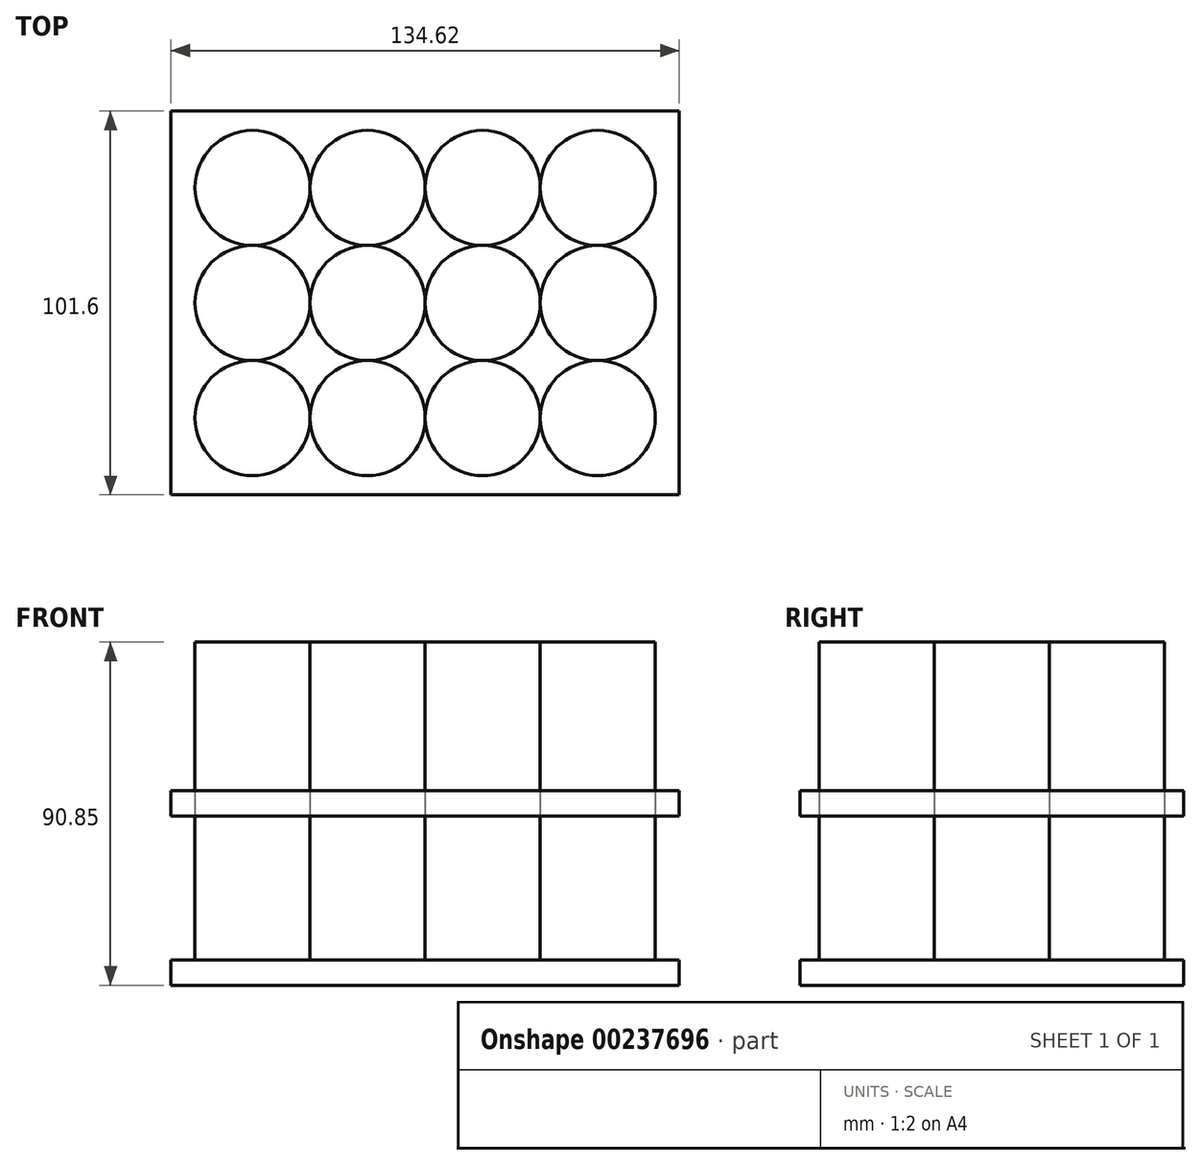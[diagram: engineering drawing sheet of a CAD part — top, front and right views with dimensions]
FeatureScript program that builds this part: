
annotation { "Feature Type Name" : "Feature", "Feature Type Description" : "" }
export const myFeature = defineFeature(function(context is Context, id is Id, definition is map)
    precondition{}
    {
        {
            var Q0;
            Q0=qCreatedBy(makeId("Top.planeOp"),FACE);
            var sketch = newSketch(context, id + "F0", { "sketchPlane" : qUnion([Q0])});
            skCircle(sketch, "E0", {"center": v(-45.72, -30.48) * mm, "radius": 15.24 * mm});
            skCircle(sketch, "E1", {"center": v(-15.24, -30.48) * mm, "radius": 15.24 * mm});
            skCircle(sketch, "E2", {"center": v(15.24, -30.48) * mm, "radius": 15.24 * mm});
            skCircle(sketch, "E3", {"center": v(-45.72, 0) * mm, "radius": 15.24 * mm});
            skCircle(sketch, "E4", {"center": v(-15.24, 0) * mm, "radius": 15.24 * mm});
            skCircle(sketch, "E5", {"center": v(15.24, 0) * mm, "radius": 15.24 * mm});
            skLineSegment(sketch, "E6", {"start": v(-45.72, 0) * mm, "end": v(-45.72, -30.48) * mm, "construction": true});
            skCircle(sketch, "E7", {"center": v(-45.72, 30.48) * mm, "radius": 15.24 * mm});
            skCircle(sketch, "E8", {"center": v(-15.24, 30.48) * mm, "radius": 15.24 * mm});
            skCircle(sketch, "E9", {"center": v(15.24, 30.48) * mm, "radius": 15.24 * mm});
            skLineSegment(sketch, "E10", {"start": v(-45.72, 30.48) * mm, "end": v(-45.72, 0) * mm, "construction": true});
            skCircle(sketch, "E11", {"center": v(45.72, -30.48) * mm, "radius": 15.24 * mm});
            skCircle(sketch, "E12", {"center": v(45.72, 0) * mm, "radius": 15.24 * mm});
            skCircle(sketch, "E13", {"center": v(45.72, 30.48) * mm, "radius": 15.24 * mm});
            skLineSegment(sketch, "E14", {"start": v(45.72, 30.48) * mm, "end": v(45.72, -30.48) * mm, "construction": true});
            skLineSegment(sketch, "E15", {"start": v(-45.72, 0) * mm, "end": v(45.72, 0) * mm, "construction": true});
            skLineSegment(sketch, "E16", {"start": v(-45.72, 30.48) * mm, "end": v(45.72, 30.48) * mm, "construction": true});
            skLineSegment(sketch, "E17", {"start": v(-45.72, -30.48) * mm, "end": v(45.72, -30.48) * mm, "construction": true});
            skSolve(sketch);
        }
        {
            var Q0;
            {var subQ0=sQuery(id+"F0.wireOp",EDGE,"ICpDPUjX-ivMe-23Ei-ieje-qIsjfVPonkm3");var subQ1=makeQuery(id+"F0.imprint","INTERSECT",VERTEX,{"derivedFrom":[subQ0,sQuery(id+"F0.wireOp",EDGE,"1585de0c-b4fc-4455-9636-1ccd38715f07")]});Q0=makeQuery(id+"F0.imprint","IMPRINT",FACE,{"disambiguationData":[TD([[makeQuery(id+"F0.imprint","IMPRINT",EDGE,{"disambiguationData":[TD([[subQ1,-1.0]])],"derivedFrom":subQ0}),1.0]])]});}
            var Q1;
            {var subQ0=sQuery(id+"F0.wireOp",EDGE,"1585de0c-b4fc-4455-9636-1ccd38715f07");var subQ1=makeQuery(id+"F0.imprint","INTERSECT",VERTEX,{"derivedFrom":[sQuery(id+"F0.wireOp",EDGE,"ICpDPUjX-ivMe-23Ei-ieje-qIsjfVPonkm3"),subQ0]});Q1=makeQuery(id+"F0.imprint","IMPRINT",FACE,{"disambiguationData":[TD([[makeQuery(id+"F0.imprint","IMPRINT",EDGE,{"disambiguationData":[TD([[subQ1,1.0]])],"derivedFrom":subQ0}),1.0]])]});}
            var Q2;
            {var subQ0=sQuery(id+"F0.wireOp",EDGE,"8cf919d0-c88a-4376-973f-18324e1bfcb2");var subQ1=makeQuery(id+"F0.imprint","INTERSECT",VERTEX,{"derivedFrom":[sQuery(id+"F0.wireOp",EDGE,"1585de0c-b4fc-4455-9636-1ccd38715f07"),subQ0]});Q2=makeQuery(id+"F0.imprint","IMPRINT",FACE,{"disambiguationData":[TD([[makeQuery(id+"F0.imprint","IMPRINT",EDGE,{"disambiguationData":[TD([[subQ1,-1.0]])],"derivedFrom":subQ0}),1.0]])]});}
            var Q3;
            {var subQ0=sQuery(id+"F0.wireOp",EDGE,"0c448a11-c32a-4d7b-bc3d-f4b18554e8e6");var subQ1=makeQuery(id+"F0.imprint","INTERSECT",VERTEX,{"derivedFrom":[sQuery(id+"F0.wireOp",EDGE,"8cf919d0-c88a-4376-973f-18324e1bfcb2"),subQ0]});Q3=makeQuery(id+"F0.imprint","IMPRINT",FACE,{"disambiguationData":[TD([[makeQuery(id+"F0.imprint","IMPRINT",EDGE,{"disambiguationData":[TD([[subQ1,-1.0]])],"derivedFrom":subQ0}),1.0]])]});}
            var Q4;
            {var subQ0=sQuery(id+"F0.wireOp",EDGE,"877ee094-fdc9-495d-ab0e-c5a52c05f9cd");var subQ4=makeQuery(id+"F0.imprint","INTERSECT",VERTEX,{"derivedFrom":[sQuery(id+"F0.wireOp",EDGE,"8cf919d0-c88a-4376-973f-18324e1bfcb2"),subQ0]});Q4=makeQuery(id+"F0.imprint","IMPRINT",FACE,{"disambiguationData":[TD([[makeQuery(id+"F0.imprint","IMPRINT",EDGE,{"disambiguationData":[TD([[subQ4,1.0]])],"derivedFrom":subQ0}),1.0]])]});}
            var Q5;
            {var subQ0=sQuery(id+"F0.wireOp",EDGE,"d8245553-00ec-417b-91d8-0db8256ae251");var subQ4=makeQuery(id+"F0.imprint","INTERSECT",VERTEX,{"derivedFrom":[sQuery(id+"F0.wireOp",EDGE,"1585de0c-b4fc-4455-9636-1ccd38715f07"),subQ0]});Q5=makeQuery(id+"F0.imprint","IMPRINT",FACE,{"disambiguationData":[TD([[makeQuery(id+"F0.imprint","IMPRINT",EDGE,{"disambiguationData":[TD([[subQ4,1.0]])],"derivedFrom":subQ0}),1.0]])]});}
            var Q6;
            {var subQ0=sQuery(id+"F0.wireOp",EDGE,"E0");var subQ1=makeQuery(id+"F0.imprint","INTERSECT",VERTEX,{"derivedFrom":[sQuery(id+"F0.wireOp",EDGE,"d8245553-00ec-417b-91d8-0db8256ae251"),subQ0]});Q6=makeQuery(id+"F0.imprint","IMPRINT",FACE,{"disambiguationData":[TD([[makeQuery(id+"F0.imprint","IMPRINT",EDGE,{"disambiguationData":[TD([[subQ1,1.0]])],"derivedFrom":subQ0}),1.0]])]});}
            var Q7;
            {var subQ0=sQuery(id+"F0.wireOp",EDGE,"E1");var subQ1=makeQuery(id+"F0.imprint","INTERSECT",VERTEX,{"derivedFrom":[subQ0,sQuery(id+"F0.wireOp",EDGE,"E2")]});Q7=makeQuery(id+"F0.imprint","IMPRINT",FACE,{"disambiguationData":[TD([[makeQuery(id+"F0.imprint","IMPRINT",EDGE,{"disambiguationData":[TD([[subQ1,-1.0]])],"derivedFrom":subQ0}),1.0]])]});}
            var Q8;
            {var subQ0=sQuery(id+"F0.wireOp",EDGE,"E2");var subQ1=makeQuery(id+"F0.imprint","INTERSECT",VERTEX,{"derivedFrom":[sQuery(id+"F0.wireOp",EDGE,"0c448a11-c32a-4d7b-bc3d-f4b18554e8e6"),subQ0]});Q8=makeQuery(id+"F0.imprint","IMPRINT",FACE,{"disambiguationData":[TD([[makeQuery(id+"F0.imprint","IMPRINT",EDGE,{"disambiguationData":[TD([[subQ1,-1.0]])],"derivedFrom":subQ0}),1.0]])]});}
            var Q9;
            {var subQ0=sQuery(id+"F0.wireOp",EDGE,"E3");var subQ1=makeQuery(id+"F0.imprint","INTERSECT",VERTEX,{"derivedFrom":[sQuery(id+"F0.wireOp",EDGE,"E0"),subQ0]});Q9=makeQuery(id+"F0.imprint","IMPRINT",FACE,{"disambiguationData":[TD([[makeQuery(id+"F0.imprint","IMPRINT",EDGE,{"disambiguationData":[TD([[subQ1,1.0]])],"derivedFrom":subQ0}),1.0]])]});}
            var Q10;
            {var subQ0=sQuery(id+"F0.wireOp",EDGE,"E4");var subQ1=makeQuery(id+"F0.imprint","INTERSECT",VERTEX,{"derivedFrom":[sQuery(id+"F0.wireOp",EDGE,"E3"),subQ0]});Q10=makeQuery(id+"F0.imprint","IMPRINT",FACE,{"disambiguationData":[TD([[makeQuery(id+"F0.imprint","IMPRINT",EDGE,{"disambiguationData":[TD([[subQ1,1.0]])],"derivedFrom":subQ0}),1.0]])]});}
            var Q11;
            {var subQ0=sQuery(id+"F0.wireOp",EDGE,"E5");var subQ1=makeQuery(id+"F0.imprint","INTERSECT",VERTEX,{"derivedFrom":[sQuery(id+"F0.wireOp",EDGE,"E2"),subQ0]});Q11=makeQuery(id+"F0.imprint","IMPRINT",FACE,{"disambiguationData":[TD([[makeQuery(id+"F0.imprint","IMPRINT",EDGE,{"disambiguationData":[TD([[subQ1,1.0]])],"derivedFrom":subQ0}),1.0]])]});}
            var Q12;
            Q12=makeQuery(id+"F0.imprint","IMPRINT",FACE,{"disambiguationData":[TD([[makeQuery(id+"F0.imprint","IMPRINT",EDGE,{"derivedFrom":sQuery(id+"F0.wireOp",EDGE,"E13")}),1.0]])]});
            var Q13;
            {var subQ0=sQuery(id+"F0.wireOp",EDGE,"E11");var subQ1=makeQuery(id+"F0.imprint","INTERSECT",VERTEX,{"derivedFrom":[sQuery(id+"F0.wireOp",EDGE,"E2"),subQ0]});Q13=makeQuery(id+"F0.imprint","IMPRINT",FACE,{"disambiguationData":[TD([[makeQuery(id+"F0.imprint","IMPRINT",EDGE,{"disambiguationData":[TD([[subQ1,1.0]])],"derivedFrom":subQ0}),1.0]])]});}
            var Q14;
            {var subQ0=sQuery(id+"F0.wireOp",EDGE,"E8");var subQ1=makeQuery(id+"F0.imprint","INTERSECT",VERTEX,{"derivedFrom":[sQuery(id+"F0.wireOp",EDGE,"E7"),subQ0]});Q14=makeQuery(id+"F0.imprint","IMPRINT",FACE,{"disambiguationData":[TD([[makeQuery(id+"F0.imprint","IMPRINT",EDGE,{"disambiguationData":[TD([[subQ1,1.0]])],"derivedFrom":subQ0}),1.0]])]});}
            var Q15;
            {var subQ0=sQuery(id+"F0.wireOp",EDGE,"E7");var subQ1=makeQuery(id+"F0.imprint","INTERSECT",VERTEX,{"derivedFrom":[sQuery(id+"F0.wireOp",EDGE,"E3"),subQ0]});Q15=makeQuery(id+"F0.imprint","IMPRINT",FACE,{"disambiguationData":[TD([[makeQuery(id+"F0.imprint","IMPRINT",EDGE,{"disambiguationData":[TD([[subQ1,1.0]])],"derivedFrom":subQ0}),1.0]])]});}
            var Q16;
            {var subQ0=sQuery(id+"F0.wireOp",EDGE,"E12");var subQ1=makeQuery(id+"F0.imprint","INTERSECT",VERTEX,{"derivedFrom":[subQ0,sQuery(id+"F0.wireOp",EDGE,"E13")]});Q16=makeQuery(id+"F0.imprint","IMPRINT",FACE,{"disambiguationData":[TD([[makeQuery(id+"F0.imprint","IMPRINT",EDGE,{"disambiguationData":[TD([[subQ1,-1.0]])],"derivedFrom":subQ0}),1.0]])]});}
            var Q17;
            {var subQ0=sQuery(id+"F0.wireOp",EDGE,"E9");var subQ1=makeQuery(id+"F0.imprint","INTERSECT",VERTEX,{"derivedFrom":[sQuery(id+"F0.wireOp",EDGE,"E8"),subQ0]});Q17=makeQuery(id+"F0.imprint","IMPRINT",FACE,{"disambiguationData":[TD([[makeQuery(id+"F0.imprint","IMPRINT",EDGE,{"disambiguationData":[TD([[subQ1,1.0]])],"derivedFrom":subQ0}),1.0]])]});}
            var Q18;
            Q18=sQuery(id+"F0.wireOp",EDGE,"877ee094-fdc9-495d-ab0e-c5a52c05f9cd");
            var Q19;
            Q19=sQuery(id+"F0.wireOp",EDGE,"ICpDPUjX-ivMe-23Ei-ieje-qIsjfVPonkm3");
            var Q20;
            Q20=sQuery(id+"F0.wireOp",EDGE,"E2");
            var Q21;
            Q21=sQuery(id+"F0.wireOp",EDGE,"E1");
            var Q22;
            Q22=sQuery(id+"F0.wireOp",EDGE,"E0");
            var Q23;
            Q23=sQuery(id+"F0.wireOp",EDGE,"0c448a11-c32a-4d7b-bc3d-f4b18554e8e6");
            var Q24;
            Q24=sQuery(id+"F0.wireOp",EDGE,"d8245553-00ec-417b-91d8-0db8256ae251");
            var Q25;
            Q25=sQuery(id+"F0.wireOp",EDGE,"8cf919d0-c88a-4376-973f-18324e1bfcb2");
            var Q26;
            Q26=sQuery(id+"F0.wireOp",EDGE,"1585de0c-b4fc-4455-9636-1ccd38715f07");
            extrude(context, id + "F1", {"entities" : qUnion([Q0, Q1, Q2, Q3, Q4, Q5, Q6, Q7, Q8, Q9, Q10, Q11, Q12, Q13, Q14, Q15, Q16, Q17]), "surfaceEntities" : qUnion([Q18, Q19, Q20, Q21, Q22, Q23, Q24, Q25, Q26]), "depth" : 84.16 * mm});
        }
        {
            var Q0;
            Q0=qCreatedBy(makeId("Front.planeOp"),FACE);
            var sketch = newSketch(context, id + "F2", { "sketchPlane" : qUnion([Q0])});
            skLineSegment(sketch, "E18.bottom", {"start": v(67.31, 0) * mm, "end": v(-67.31, 0) * mm});
            skLineSegment(sketch, "E18.top", {"start": v(67.31, -6.7) * mm, "end": v(-67.31, -6.7) * mm});
            skLineSegment(sketch, "E18.left", {"start": v(67.31, 0) * mm, "end": v(67.31, -6.7) * mm});
            skLineSegment(sketch, "E18.right", {"start": v(-67.31, 0) * mm, "end": v(-67.31, -6.7) * mm});
            skLineSegment(sketch, "E19", {"start": v(-45.8, 38.1) * mm, "end": v(45.84, 38.1) * mm, "construction": true});
            skLineSegment(sketch, "E20.bottom", {"start": v(67.31, 44.8) * mm, "end": v(-67.31, 44.8) * mm});
            skLineSegment(sketch, "E20.top", {"start": v(67.31, 38.1) * mm, "end": v(-67.31, 38.1) * mm});
            skLineSegment(sketch, "E20.left", {"start": v(67.31, 44.8) * mm, "end": v(67.31, 38.1) * mm});
            skLineSegment(sketch, "E20.right", {"start": v(-67.31, 44.8) * mm, "end": v(-67.31, 38.1) * mm});
            skLineSegment(sketch, "E21", {"start": v(67.31, -6.7) * mm, "end": v(67.3, 38.1) * mm, "construction": true});
            skLineSegment(sketch, "E22", {"start": v(-67.31, 58.76) * mm, "end": v(-67.31, 44.8) * mm, "construction": true});
            skSolve(sketch);
        }
        {
            var Q0;
            Q0=makeQuery(id+"F2.imprint","IMPRINT",FACE,{"disambiguationData":[TD([[makeQuery(id+"F2.imprint","IMPRINT",EDGE,{"derivedFrom":sQuery(id+"F2.wireOp",EDGE,"E18.bottom")}),1.0]])]});
            var Q1;
            Q1=makeQuery(id+"F2.imprint","IMPRINT",FACE,{"disambiguationData":[TD([[makeQuery(id+"F2.imprint","IMPRINT",EDGE,{"derivedFrom":sQuery(id+"F2.wireOp",EDGE,"E20.bottom")}),1.0]])]});
            var Q2;
            Q2=makeQuery(id+"F2.imprint","IMPRINT",FACE,{"disambiguationData":[TD([[makeQuery(id+"F2.imprint","IMPRINT",EDGE,{"derivedFrom":sQuery(id+"F2.wireOp",EDGE,"8b0a0e72-80e0-4632-a41d-e0e877318674.bottom")}),1.0]])]});
            var Q3;
            Q3=sQuery(id+"F2.wireOp",EDGE,"E18.bottom");
            extrude(context, id + "F3", {"entities" : qUnion([Q0, Q1, Q2]), "surfaceEntities" : qUnion([Q3]), "endBound" : BoundingType.SYMMETRIC, "oppositeDirection" : true, "depth" : 101.6 * mm});
        }
    });
